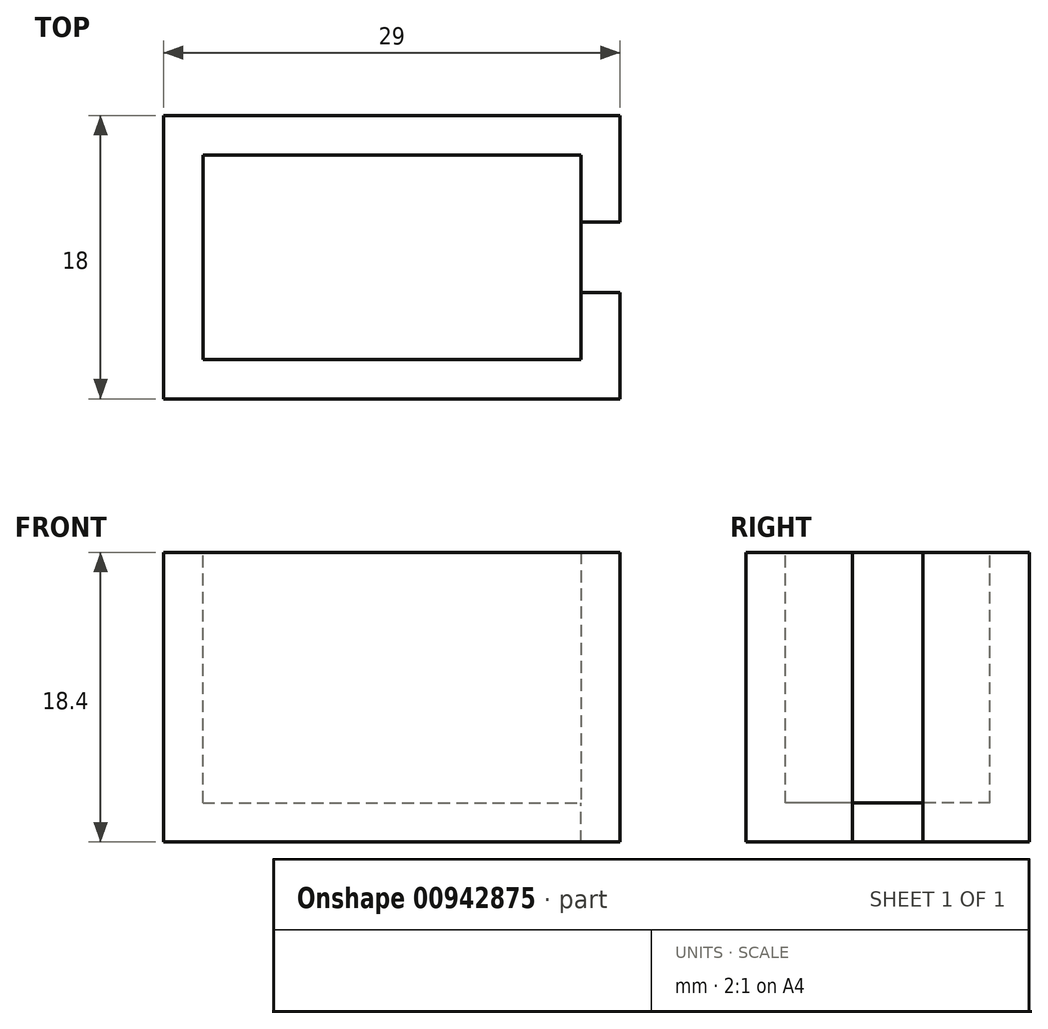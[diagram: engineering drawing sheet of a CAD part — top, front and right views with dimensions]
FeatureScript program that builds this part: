
annotation { "Feature Type Name" : "Feature", "Feature Type Description" : "" }
export const myFeature = defineFeature(function(context is Context, id is Id, definition is map)
    precondition{}
    {
        {
            var Q0;
            Q0=qCreatedBy(makeId("Top.planeOp"),FACE);
            var sketch = newSketch(context, id + "F0", { "sketchPlane" : qUnion([Q0])});
            skLineSegment(sketch, "E0.bottom", {"start": v(-19.2, -10.17) * mm, "end": v(4.8, -10.17) * mm});
            skLineSegment(sketch, "E0.top", {"start": v(-19.2, -23.17) * mm, "end": v(4.8, -23.17) * mm});
            skLineSegment(sketch, "E0.left", {"start": v(-19.2, -10.17) * mm, "end": v(-19.2, -23.17) * mm});
            skLineSegment(sketch, "E0.right", {"start": v(4.8, -10.17) * mm, "end": v(4.8, -23.17) * mm});
            skSolve(sketch);
        }
        {
            var Q0;
            Q0=makeQuery(id+"F0.imprint","IMPRINT",FACE,{"disambiguationData":[TD([[makeQuery(id+"F0.imprint","IMPRINT",EDGE,{"derivedFrom":sQuery(id+"F0.wireOp",EDGE,"E0.bottom")}),-1.0]])]});
            extrude(context, id + "F1", {"entities" : qUnion([Q0]), "oppositeDirection" : true, "depth" : 15.9 * mm, "offsetDistance" : 25 * mm});
        }
        {
            var Q0;
            Q0=makeQuery(id+"F1.opExtrude","CAP_FACE",FACE,{"disambiguationData":[OSD([sQuery(id+"F0.wireOp",EDGE,"E0.bottom"),sQuery(id+"F0.wireOp",EDGE,"E0.top"),sQuery(id+"F0.wireOp",EDGE,"E0.left"),sQuery(id+"F0.wireOp",EDGE,"E0.right")])],"isStart":true});
            shell(context, id + "F2", {"entities" : qUnion([Q0]), "thickness" : 2.5 * mm, "oppositeDirection" : true});
        }
        {
            var Q0;
            Q0=makeQuery(id+"F1.opExtrude","SWEPT_FACE",FACE,{"disambiguationData":[OSD([sQuery(id+"F0.wireOp",EDGE,"E0.right")])]});
            var sketch = newSketch(context, id + "F3", { "sketchPlane" : qUnion([Q0])});
            skLineSegment(sketch, "E1", {"start": v(-16.67, 0) * mm, "end": v(-14.42, 0) * mm});
            skLineSegment(sketch, "E2", {"start": v(-14.42, 0) * mm, "end": v(-14.42, -18.4) * mm});
            skLineSegment(sketch, "E3", {"start": v(-14.42, -18.4) * mm, "end": v(-18.92, -18.4) * mm});
            skLineSegment(sketch, "E4", {"start": v(-18.92, -18.4) * mm, "end": v(-18.92, 0) * mm});
            skLineSegment(sketch, "E5", {"start": v(-18.92, 0) * mm, "end": v(-16.67, 0) * mm});
            skSolve(sketch);
        }
        {
            var Q0;
            Q0=makeQuery(id+"F3.imprint","IMPRINT",FACE,{"disambiguationData":[TD([[makeQuery(id+"F3.imprint","IMPRINT",EDGE,{"derivedFrom":sQuery(id+"F3.wireOp",EDGE,"E1")}),1.0]])]});
            extrude(context, id + "F4", {"entities" : qUnion([Q0]), "operationType" : NewBodyOperationType.REMOVE, "oppositeDirection" : true, "depth" : 2.5 * mm, "offsetDistance" : 25 * mm});
        }
    });
